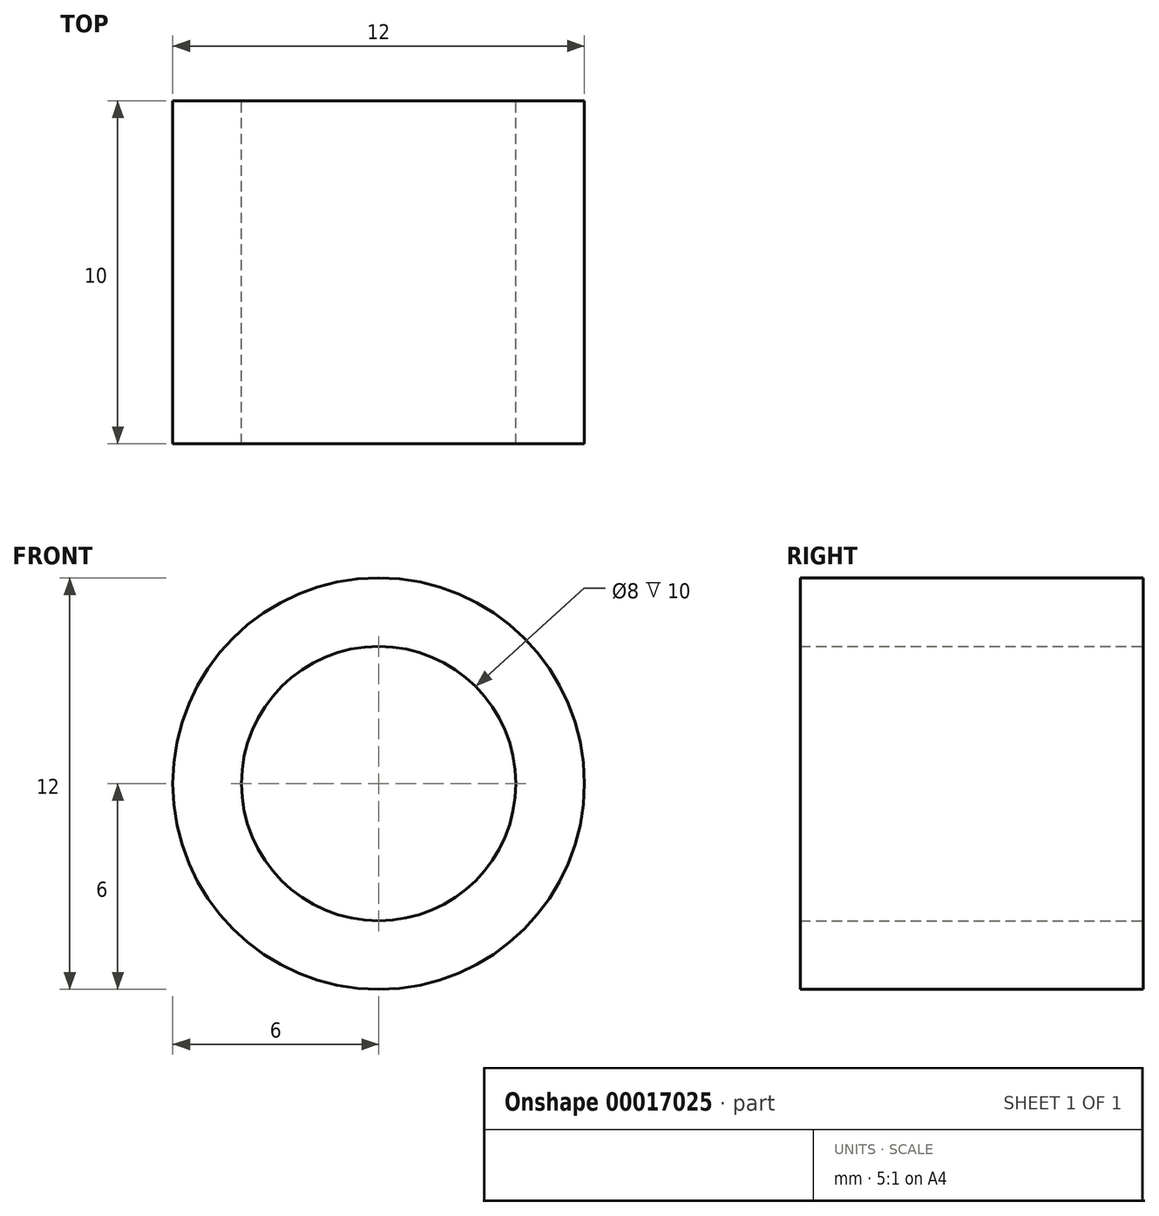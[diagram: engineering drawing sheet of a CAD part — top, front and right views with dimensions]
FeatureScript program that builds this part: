
annotation { "Feature Type Name" : "Feature", "Feature Type Description" : "" }
export const myFeature = defineFeature(function(context is Context, id is Id, definition is map)
    precondition{}
    {
        {
            var Q0;
            Q0=qCreatedBy(makeId("Front.planeOp"),FACE);
            var sketch = newSketch(context, id + "F0", { "sketchPlane" : qUnion([Q0])});
            skCircle(sketch, "E0", {"center": v(0, 0) * mm, "radius": 6 * mm});
            skCircle(sketch, "E1", {"center": v(0, 0) * mm, "radius": 4 * mm});
            skSolve(sketch);
        }
        {
            var Q0;
            Q0 = qSketchRegion(id + "F0", true);
            extrude(context, id + "F1", {"entities" : qUnion([Q0]), "depth" : 10 * mm});
        }
    });
